# Revit family: PRD_AR_MltFnctnDspnsrs_FX-MWashPlaceUnit_FXCD1001M_FXCT1001M
name_source: partatom
category: Specialty Equipment
revit_build: Autodesk Revit 2018 (Build: 20190510_1515(x64)
units: mm (PartAtom-declared; Revit-internal decimal feet)

## family parameters
Cut with Voids When Loaded = Yes
Host = Face
OmniClass Number = 23.40.20.21.34
OmniClass Title = Soap Holders, Dispensers
Part Type = Normal
Room Calculation Point = No
Round Connector Dimension = Use Diameter
Shared = No

## types (2) — shared parameters
ApparentLoad = 0 VA
AssetType = Fixed
Category = Pr_40_70_22_52, Multi-function dispensers
Color = white
Default Elevation = 1000 mm  [stored 3.28084 ft]
DiameterNominal = 15  [stored 0.0492126 ft]
DispenserMaterial = PRD_AR_Steel_PowderCoated_White
DrainSize = 32  [stored 0.104987 ft]
DurationUnit = year
Finish = powder coated
FlowColdWater = 0.0 L/s
FlowHotWater = 0.0 L/s
GrossWeight = 36.50 kg
IfcExportAs = IfcFurnitureType
IfcExportType = USERDEFINED
IsBuiltIn = TRUE
MainColor = stainless steel
Manufacturer = KWC Group AG
ManufacturerName = KWC Group AG
ManufacturerURL = www.kwc.com
Material = stainless steel
MinimumFlowPressure = 1.0 bar
NBSDescription = Multi-function dispensers
NBSReference = 45-35-72/384
NetWeight = 32.50 kg
NominalDepth = 206 mm  [stored 0.675853 ft]
NominalHeight = 903 mm  [stored 2.9626 ft]
NominalWidth = 600 mm
OverallPower = 1000 W
PanelMaterial = PRD_AR_Glass
PowerFactor = 1
ProductInformation = https://pim.kwc.com
ProtectionDegree = IPX1
Size = 600 x 903 x 206 mm
SupplyVoltage = 230 V AC, 50/60 Hz
TailorMade = No
URL = www.kwc.com
Uniclass2015Code = Pr_40_70_22_52
Uniclass2015Title = Multi-function dispensers
Uniclass2015Version = Products v1.23
Version = 1
Voltage = 0 V
VolumeFlowRate = 6 l/min at 3 bar
WarrantyDurationUnit = year

## per-type parameters (varying)
| type | BIMObjectName | Description | FXCD1001M | FXCT1001M | Features | FillVolumeOfPaperTowelDispenser | HandDryerAirVelocity | HandDryerAirVolume | ModelNumber | Name | PowerConsumption | PowerSupplyConnection | ProductCode | ProtectiveSystemIP |
| FXCD1001M | PRD_AR_MultiFunctionDispensers_FX-MWashPlaceUnitWater-Soap-Air_FXCD1001M | FX-M wash place unit Water-Soap-Air for wall mounting, touch free optoelectronically controlled. For hot and cold water connectivity. Thermostat for mounting onto angle valve with installation set for preset delivery of premixed hot water, soap pump for liquid soap and hand dryer. Lighting up of pictograms above the respective sensor position as well as start of wash place lighting indicate user detection. The pictogram of the active function is illuminated maximally. Cabinet housing made of powder coated stainless steel, white, mirrored door, door hinge left and cylinder lock. | Yes | No | Water-Soap-Air |  | 95-115 m/s | 80 m3/h | 2030063219 | FX-M wash place unit Water-Soap-Air FXCD1001M | 1200 | 230 V AC | 204.0653.927 | 20 |
| FXCT1001M | PRD_AR_MultiFunctionDispensers_FX-MWashPlaceUnitWater-Soap-PaperTowelDispenser_FXCT1001M | FX-M wash place unit Water-Soap-Paper towel dispenser for wall mounting, touch free opto-electronically controlled. For hot and cold water connectivity. Thermostat for mounting onto angle valve with installation set for preset delivery of premixed hot water, soap pump for liquid soap and paper towel dispenser. Lighting up of pictograms above the respective sensor position as well as start of wash place lighting indicate user detection. The pictogram of the active function is illuminated maximally. Cabinet housing made of powder coated stainless steel, white, mirrored door, door hinge left and cylinder lock. | No | Yes | Water-Soap-Paper towel | 300 - 400 pieces (H2 - format with Z - folding) |  |  | 2030065018 | FX-M wash place unit Water-Soap-Paper towel dispenser FXCT1001M |  |  | 204.0653.926 |  |

note: column(s) folded — value = type name in every type: Model, ModelReference

note: [stored X ft] marks values corroborated as IEEE doubles in the binary element streams (Revit-internal decimal feet)

## geometry (parser evidence)
native form markers: Sweep x13
no freeform markers — native parametric forms only
